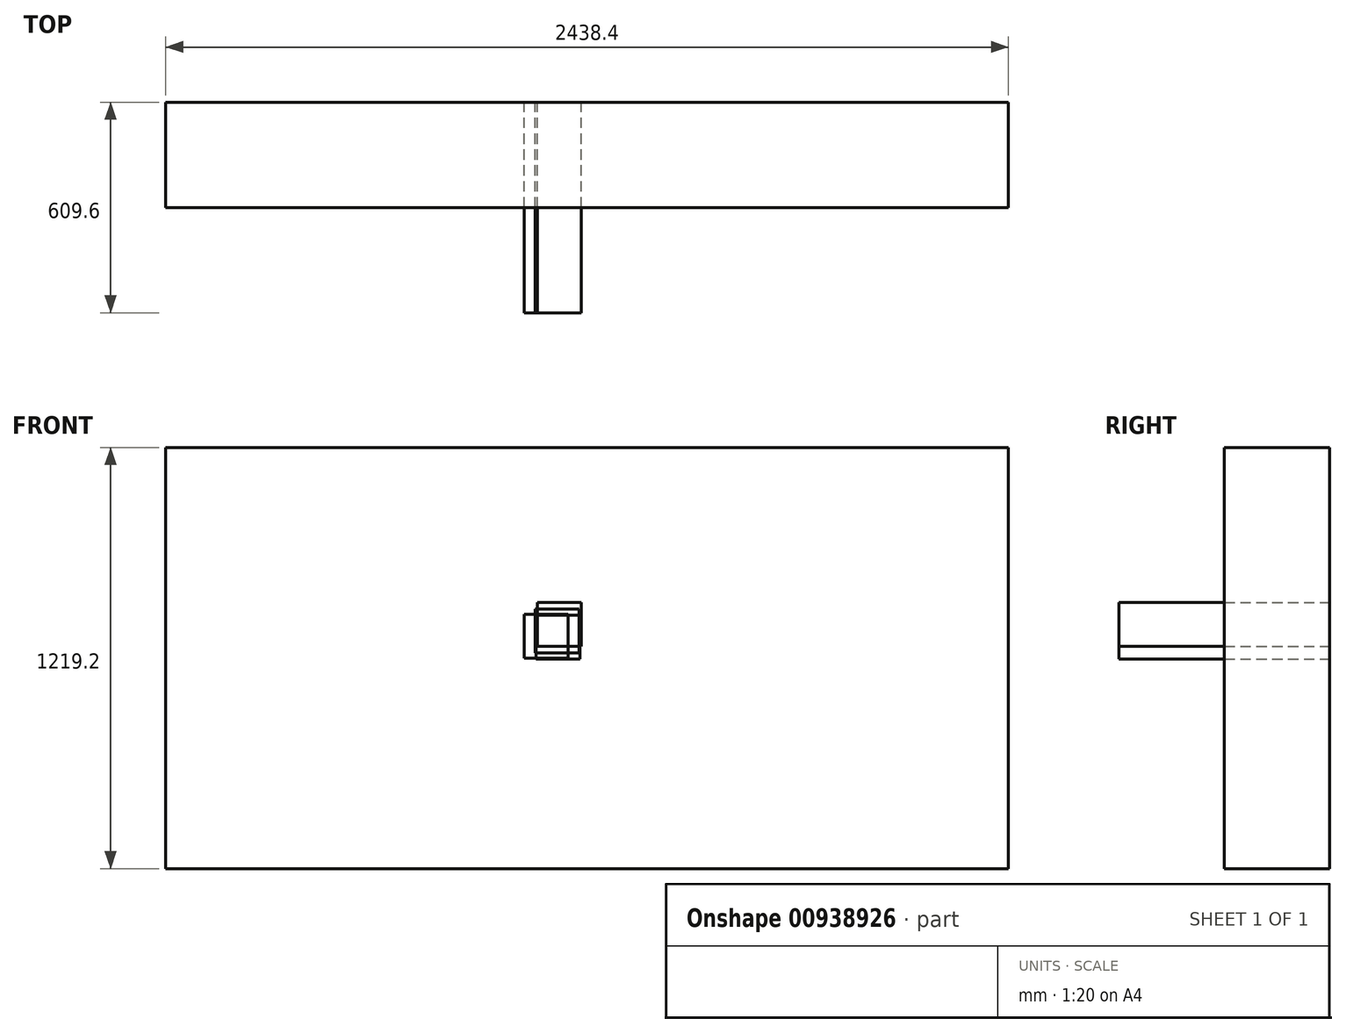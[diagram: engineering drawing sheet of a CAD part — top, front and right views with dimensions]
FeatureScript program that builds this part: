
annotation { "Feature Type Name" : "Feature", "Feature Type Description" : "" }
export const myFeature = defineFeature(function(context is Context, id is Id, definition is map)
    precondition{}
    {
        {
            var Q0;
            Q0=qCreatedBy(makeId("Front.planeOp"),FACE);
            var sketch = newSketch(context, id + "F0", { "sketchPlane" : qUnion([Q0])});
            skLineSegment(sketch, "E0.bottom", {"start": v(1219.2, 609.6) * mm, "end": v(-1219.2, 609.6) * mm});
            skLineSegment(sketch, "E0.top", {"start": v(1219.2, -609.6) * mm, "end": v(-1219.2, -609.6) * mm});
            skLineSegment(sketch, "E0.left", {"start": v(1219.2, 609.6) * mm, "end": v(1219.2, -609.6) * mm});
            skLineSegment(sketch, "E0.right", {"start": v(-1219.2, 609.6) * mm, "end": v(-1219.2, -609.6) * mm});
            skPoint(sketch, "E0.middle", {"position": v(0, 0) * mm});
            skLineSegment(sketch, "E1.0", {"start": v(-1225.55, 615.95) * mm, "end": v(-1225.55, -609.6) * mm});
            skLineSegment(sketch, "E1.1", {"start": v(1225.55, 615.95) * mm, "end": v(-1225.55, 615.95) * mm});
            skLineSegment(sketch, "E1.2", {"start": v(1225.55, 615.95) * mm, "end": v(1225.55, -609.6) * mm});
            skSolve(sketch);
        }
        {
            var Q0;
            Q0=makeQuery(id+"F0.imprint","IMPRINT",FACE,{"disambiguationData":[TD([[makeQuery(id+"F0.imprint","IMPRINT",EDGE,{"derivedFrom":sQuery(id+"F0.wireOp",EDGE,"E0.bottom")}),1.0]])]});
            extrude(context, id + "F1", {"entities" : qUnion([Q0]), "depth" : 304.8 * mm, "offsetDistance" : 25.4 * mm});
        }
        {
            var Q0;
            Q0=qCreatedBy(makeId("Front.planeOp"),FACE);
            var sketch = newSketch(context, id + "F2", { "sketchPlane" : qUnion([Q0])});
            skLineSegment(sketch, "E2.bottom", {"start": v(-143.74, 160.7) * mm, "end": v(-16.74, 160.7) * mm});
            skLineSegment(sketch, "E2.top", {"start": v(-143.74, 33.7) * mm, "end": v(-16.74, 33.7) * mm});
            skLineSegment(sketch, "E2.left", {"start": v(-143.74, 160.7) * mm, "end": v(-143.74, 33.7) * mm});
            skLineSegment(sketch, "E2.right", {"start": v(-16.74, 160.7) * mm, "end": v(-16.74, 33.7) * mm});
            skSolve(sketch);
        }
        {
            var Q0;
            Q0=qCreatedBy(makeId("Front.planeOp"),FACE);
            var sketch = newSketch(context, id + "F3", { "sketchPlane" : qUnion([Q0])});
            skLineSegment(sketch, "E3.bottom", {"start": v(-182.4, 127) * mm, "end": v(-55.4, 127) * mm});
            skLineSegment(sketch, "E3.top", {"start": v(-182.4, 0) * mm, "end": v(-55.4, 0) * mm});
            skLineSegment(sketch, "E3.left", {"start": v(-182.4, 127) * mm, "end": v(-182.4, 0) * mm});
            skLineSegment(sketch, "E3.right", {"start": v(-55.4, 127) * mm, "end": v(-55.4, 0) * mm});
            skSolve(sketch);
        }
        {
            var Q0;
            Q0=qCreatedBy(makeId("Front.planeOp"),FACE);
            var sketch = newSketch(context, id + "F4", { "sketchPlane" : qUnion([Q0])});
            skLineSegment(sketch, "E4.bottom", {"start": v(-150.93, 142.18) * mm, "end": v(-23.93, 142.18) * mm});
            skLineSegment(sketch, "E4.top", {"start": v(-150.93, 15.18) * mm, "end": v(-23.93, 15.18) * mm});
            skLineSegment(sketch, "E4.left", {"start": v(-150.93, 142.18) * mm, "end": v(-150.93, 15.18) * mm});
            skLineSegment(sketch, "E4.right", {"start": v(-23.93, 142.18) * mm, "end": v(-23.93, 15.18) * mm});
            skSolve(sketch);
        }
        {
            var Q0;
            Q0=qCreatedBy(makeId("Front.planeOp"),FACE);
            var sketch = newSketch(context, id + "F5", { "sketchPlane" : qUnion([Q0])});
            skLineSegment(sketch, "E5.bottom", {"start": v(-148.2, 124) * mm, "end": v(-21.2, 124) * mm});
            skLineSegment(sketch, "E5.top", {"start": v(-148.2, -3) * mm, "end": v(-21.2, -3) * mm});
            skLineSegment(sketch, "E5.left", {"start": v(-148.2, 124) * mm, "end": v(-148.2, -3) * mm});
            skLineSegment(sketch, "E5.right", {"start": v(-21.2, 124) * mm, "end": v(-21.2, -3) * mm});
            skSolve(sketch);
        }
        {
            var Q0;
            Q0=makeQuery(id+"F2.imprint","IMPRINT",FACE,{"disambiguationData":[TD([[makeQuery(id+"F2.imprint","IMPRINT",EDGE,{"derivedFrom":sQuery(id+"F2.wireOp",EDGE,"E2.bottom")}),-1.0]])]});
            extrude(context, id + "F6", {"entities" : qUnion([Q0]), "depth" : 609.6 * mm, "offsetDistance" : 25.4 * mm});
        }
        {
            var Q0;
            Q0=makeQuery(id+"F3.imprint","IMPRINT",FACE,{"disambiguationData":[TD([[makeQuery(id+"F3.imprint","IMPRINT",EDGE,{"derivedFrom":sQuery(id+"F3.wireOp",EDGE,"E3.bottom")}),-1.0]])]});
            extrude(context, id + "F7", {"entities" : qUnion([Q0]), "depth" : 609.6 * mm, "offsetDistance" : 25.4 * mm});
        }
        {
            var Q0;
            Q0 = qSketchRegion(id + "F5", true);
            extrude(context, id + "F8", {"entities" : qUnion([Q0]), "depth" : 609.6 * mm, "offsetDistance" : 25.4 * mm});
        }
        {
            var Q0;
            Q0 = qSketchRegion(id + "F4", true);
            extrude(context, id + "F9", {"entities" : qUnion([Q0]), "depth" : 609.6 * mm, "offsetDistance" : 25.4 * mm});
        }
    });
